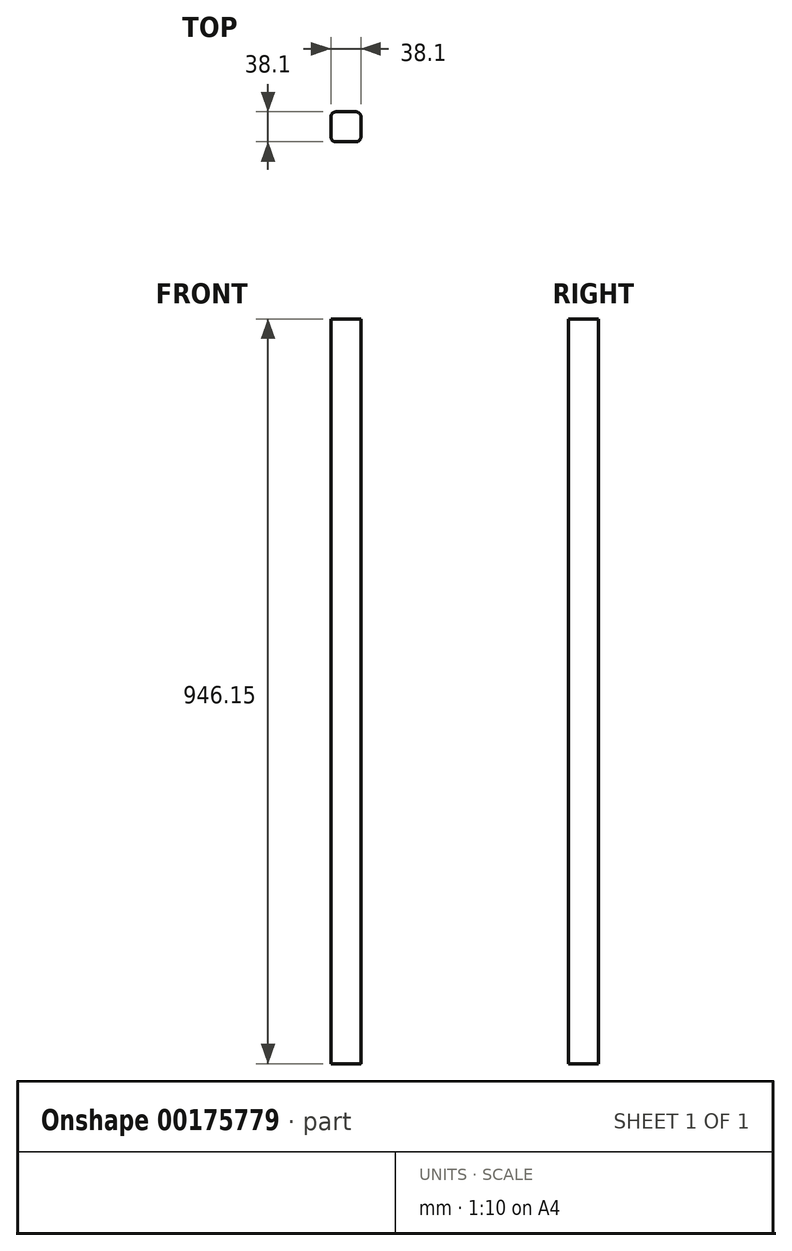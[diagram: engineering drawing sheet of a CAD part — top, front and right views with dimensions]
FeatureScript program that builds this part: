
annotation { "Feature Type Name" : "Feature", "Feature Type Description" : "" }
export const myFeature = defineFeature(function(context is Context, id is Id, definition is map)
    precondition{}
    {
        {
            var Q0;
            Q0=qCreatedBy(makeId("Top.planeOp"),FACE);
            var sketch = newSketch(context, id + "F0", { "sketchPlane" : qUnion([Q0])});
            skLineSegment(sketch, "E0.bottom", {"start": v(19.05, 19.05) * mm, "end": v(-19.05, 19.05) * mm});
            skLineSegment(sketch, "E0.top", {"start": v(19.05, -19.05) * mm, "end": v(-19.05, -19.05) * mm});
            skLineSegment(sketch, "E0.left", {"start": v(19.05, 19.05) * mm, "end": v(19.05, -19.05) * mm});
            skLineSegment(sketch, "E0.right", {"start": v(-19.05, 19.05) * mm, "end": v(-19.05, -19.05) * mm});
            skPoint(sketch, "E0.middle", {"position": v(0, 0) * mm});
            skSolve(sketch);
        }
        {
            var Q0;
            Q0=qSketchRegion(id+"F0",true);
            extrude(context, id + "F1", {"entities" : qUnion([Q0]), "depth" : 946.15 * mm, "offsetDistance" : 25.4 * mm});
        }
        {
            var Q0;
            Q0=makeQuery(id+"F1.opExtrude","SWEPT_EDGE",EDGE,{"disambiguationData":[OSD([sQuery(id+"F0.wireOp",EDGE,"E0.top"),sQuery(id+"F0.wireOp",EDGE,"E0.right")])]});
            var Q1;
            Q1=makeQuery(id+"F1.opExtrude","SWEPT_EDGE",EDGE,{"disambiguationData":[OSD([sQuery(id+"F0.wireOp",EDGE,"E0.top"),sQuery(id+"F0.wireOp",EDGE,"E0.left")])]});
            var Q2;
            Q2=makeQuery(id+"F1.opExtrude","SWEPT_EDGE",EDGE,{"disambiguationData":[OSD([sQuery(id+"F0.wireOp",EDGE,"E0.bottom"),sQuery(id+"F0.wireOp",EDGE,"E0.left")])]});
            var Q3;
            Q3=makeQuery(id+"F1.opExtrude","SWEPT_EDGE",EDGE,{"disambiguationData":[OSD([sQuery(id+"F0.wireOp",EDGE,"E0.bottom"),sQuery(id+"F0.wireOp",EDGE,"E0.right")])]});
            fillet(context, id + "F2", {"entities" : qUnion([Q0, Q1, Q2, Q3]), "radius" : 6.35 * mm, "tangentPropagation" : true, "allowEdgeOverflow" : false});
        }
    });
